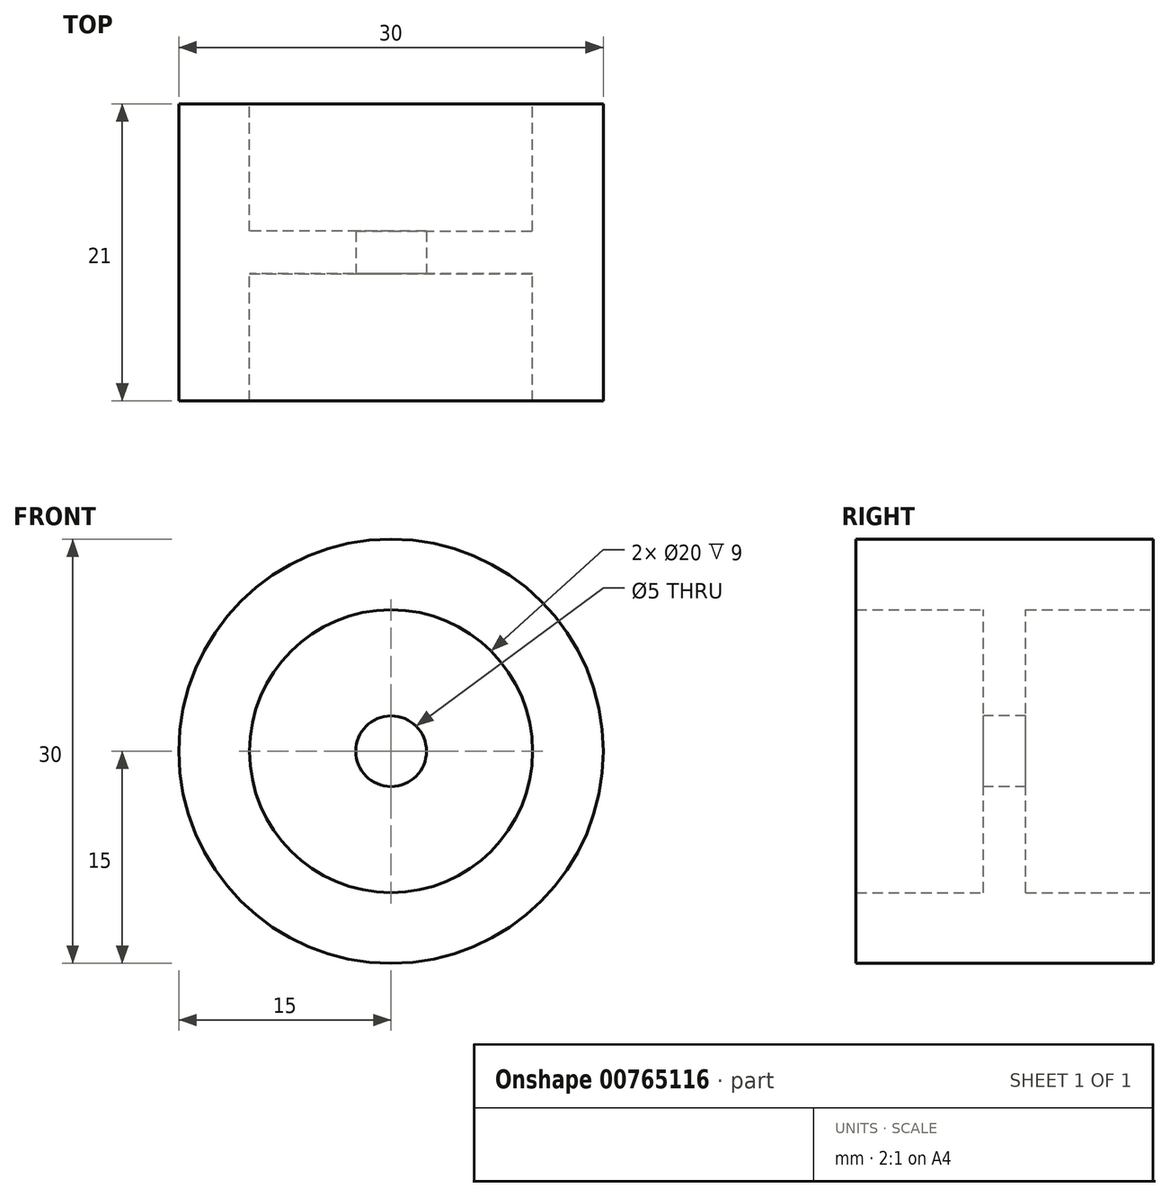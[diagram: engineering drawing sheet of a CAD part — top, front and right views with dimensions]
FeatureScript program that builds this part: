
annotation { "Feature Type Name" : "Feature", "Feature Type Description" : "" }
export const myFeature = defineFeature(function(context is Context, id is Id, definition is map)
    precondition{}
    {
        {
            var Q0;
            Q0=qCreatedBy(makeId("Front.planeOp"),FACE);
            var sketch = newSketch(context, id + "F0", { "sketchPlane" : qUnion([Q0])});
            skCircle(sketch, "E0", {"center": v(0, 0) * mm, "radius": 15 * mm});
            skSolve(sketch);
        }
        {
            var Q0;
            Q0 = qSketchRegion(id + "F0", true);
            extrude(context, id + "F1", {"entities" : qUnion([Q0]), "depth" : 12 * mm, "offsetDistance" : 25 * mm, "hasSecondDirection" : true, "secondDirectionOppositeDirection" : true, "secondDirectionDepth" : 9 * mm});
        }
        {
            var Q0;
            Q0=makeQuery(id+"F1.opExtrude","CAP_FACE",FACE,{"disambiguationData":[OSD([sQuery(id+"F0.wireOp",EDGE,"E0")])],"isStart":true});
            var sketch = newSketch(context, id + "F2", { "sketchPlane" : qUnion([Q0])});
            skPoint(sketch, "E1", {"position": v(0, 0) * mm});
            skSolve(sketch);
        }
        {
            var Q0;
            Q0=sQuery(id+"F2.wireOp",VERTEX,"E1");
            var Q1;
            Q1=makeQuery(id+"F1.opExtrude","SWEPT_BODY",BODY,{"disambiguationData":[OSD([sQuery(id+"F0.wireOp",EDGE,"E0")])]});
            hole(context, id + "F3", {"style" : HoleStyle.SIMPLE, "endStyle" : HoleEndStyle.THROUGH, "holeDiameter" : 20 * mm, "majorDiameter" : 5 * mm, "isTappedThrough" : true, "tappedDepth" : 12.7 * mm, "tapClearance" : 3, "locations" : qUnion([Q0]), "scope" : qUnion([Q1])});
        }
        {
            var Q0;
            Q0=qCreatedBy(makeId("Front.planeOp"),FACE);
            var sketch = newSketch(context, id + "F4", { "sketchPlane" : qUnion([Q0])});
            skCircle(sketch, "E2", {"center": v(0, 0) * mm, "radius": 13.57 * mm});
            skSolve(sketch);
        }
        {
            var Q0;
            Q0 = qSketchRegion(id + "F4", true);
            extrude(context, id + "F5", {"entities" : qUnion([Q0]), "operationType" : NewBodyOperationType.ADD, "depth" : 3 * mm, "offsetDistance" : 25 * mm});
        }
        {
            var Q0;
            Q0=makeQuery(id+"F5.opExtrude","CAP_FACE",FACE,{"disambiguationData":[OSD([sQuery(id+"F4.wireOp",EDGE,"E2")])],"isStart":false});
            var sketch = newSketch(context, id + "F6", { "sketchPlane" : qUnion([Q0])});
            skPoint(sketch, "E3", {"position": v(0, 0) * mm});
            skSolve(sketch);
        }
        {
            var Q0;
            Q0=sQuery(id+"F6.wireOp",VERTEX,"E3");
            var Q1;
            Q1=makeQuery(id+"F1.opExtrude","SWEPT_BODY",BODY,{"disambiguationData":[OSD([sQuery(id+"F0.wireOp",EDGE,"E0")])]});
            hole(context, id + "F7", {"style" : HoleStyle.SIMPLE, "endStyle" : HoleEndStyle.THROUGH, "holeDiameter" : 5 * mm, "majorDiameter" : 5 * mm, "isTappedThrough" : true, "tappedDepth" : 12.7 * mm, "tapClearance" : 3, "locations" : qUnion([Q0]), "scope" : qUnion([Q1])});
        }
    });
